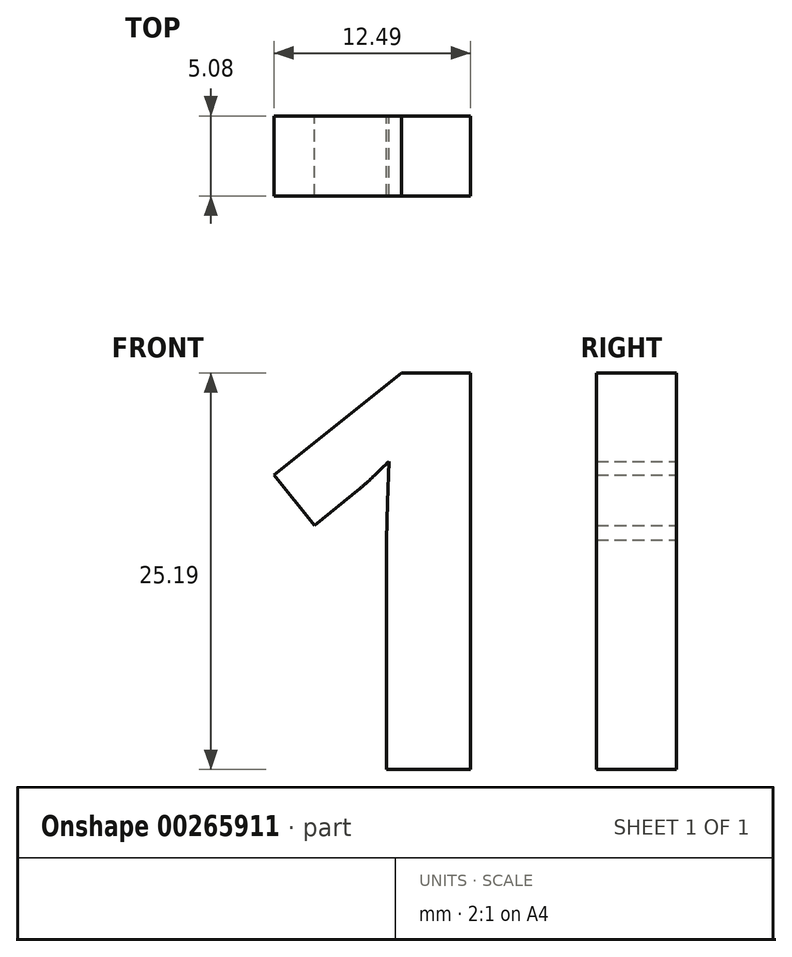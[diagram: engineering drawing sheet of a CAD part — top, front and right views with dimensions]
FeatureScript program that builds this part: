
annotation { "Feature Type Name" : "Feature", "Feature Type Description" : "" }
export const myFeature = defineFeature(function(context is Context, id is Id, definition is map)
    precondition{}
    {
        {
            var Q0;
            Q0=qCreatedBy(makeId("Front.planeOp"),FACE);
            var sketch = newSketch(context, id + "F0", { "sketchPlane" : qUnion([Q0])});
            skText(sketch, "E0", { "text": "1", "fontName": "OpenSans-Bold.ttf"});
            const initialGuessF0  = {"E0": [-0.05085, 0.01721, 1, 0, 0.0254]};
            skSetInitialGuess(sketch, initialGuessF0);
            skSolve(sketch);
        }
        {
            var Q0;
            Q0 = qSketchRegion(id + "F0", true);
            extrude(context, id + "F1", {"entities" : qUnion([Q0]), "depth" : 5.08 * mm});
        }
    });
